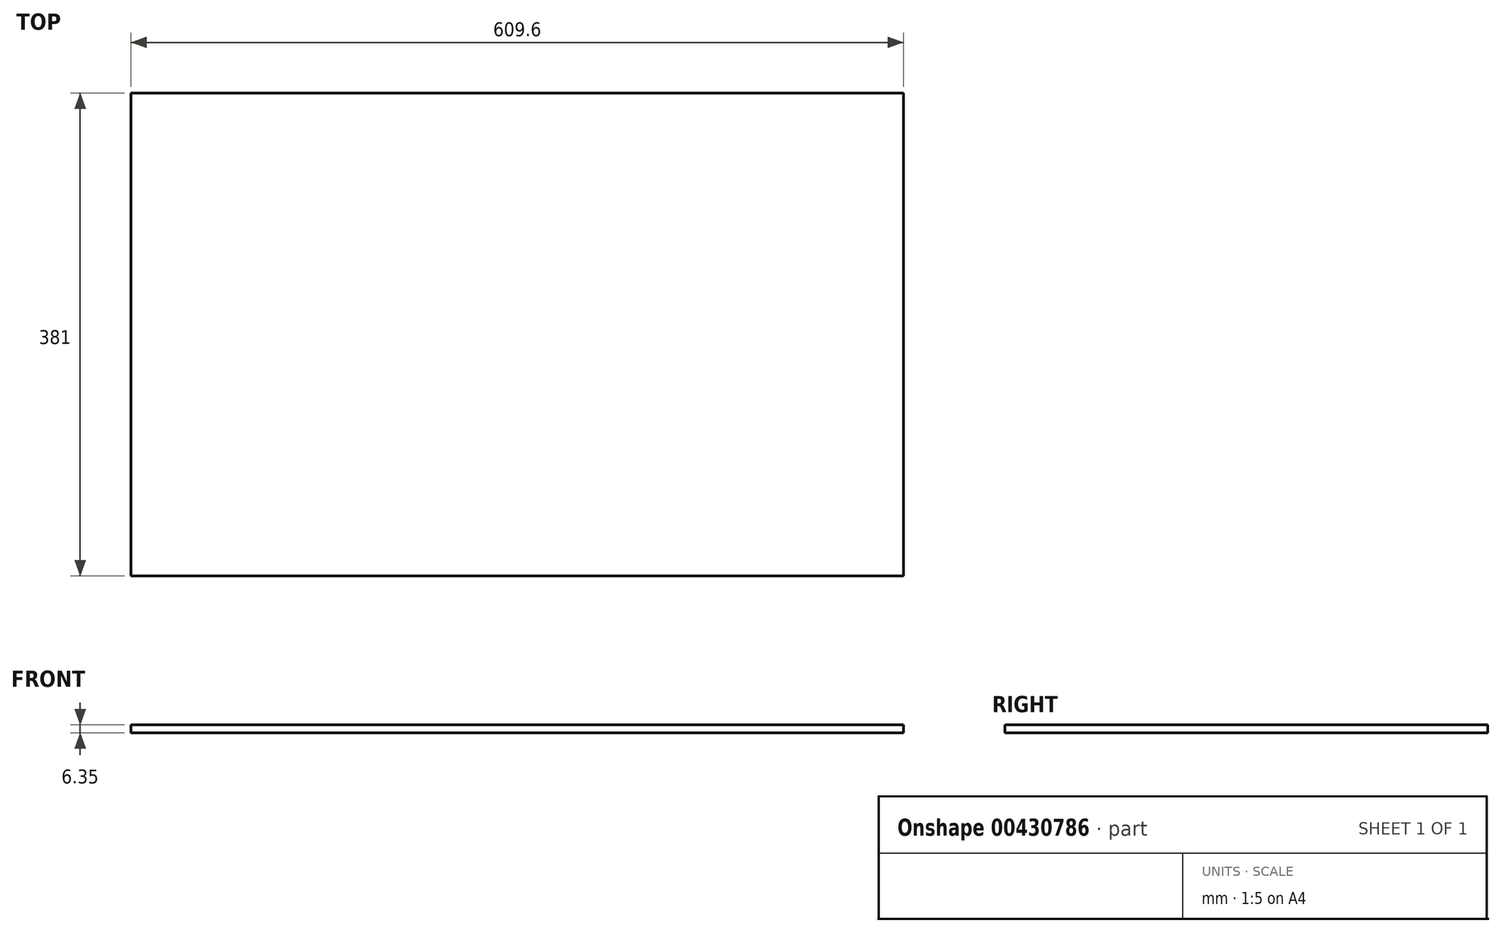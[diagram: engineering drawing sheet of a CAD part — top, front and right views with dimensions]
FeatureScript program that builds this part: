
annotation { "Feature Type Name" : "Feature", "Feature Type Description" : "" }
export const myFeature = defineFeature(function(context is Context, id is Id, definition is map)
    precondition{}
    {
        {
            var Q0;
            Q0=qCreatedBy(makeId("Top.planeOp"),FACE);
            var sketch = newSketch(context, id + "F0", { "sketchPlane" : qUnion([Q0])});
            skLineSegment(sketch, "E0.bottom", {"start": v(0, 0) * mm, "end": v(609.6, 0) * mm});
            skLineSegment(sketch, "E0.top", {"start": v(0, 381) * mm, "end": v(609.6, 381) * mm});
            skLineSegment(sketch, "E0.left", {"start": v(0, 0) * mm, "end": v(0, 381) * mm});
            skLineSegment(sketch, "E0.right", {"start": v(609.6, 0) * mm, "end": v(609.6, 381) * mm});
            skSolve(sketch);
        }
        {
            var Q0;
            Q0=makeQuery(id+"F0.imprint","IMPRINT",FACE,{"disambiguationData":[TD([[makeQuery(id+"F0.imprint","IMPRINT",EDGE,{"derivedFrom":sQuery(id+"F0.wireOp",EDGE,"E0.bottom")}),1.0]])]});
            extrude(context, id + "F1", {"entities" : qUnion([Q0]), "depth" : 6.35 * mm});
        }
    });
